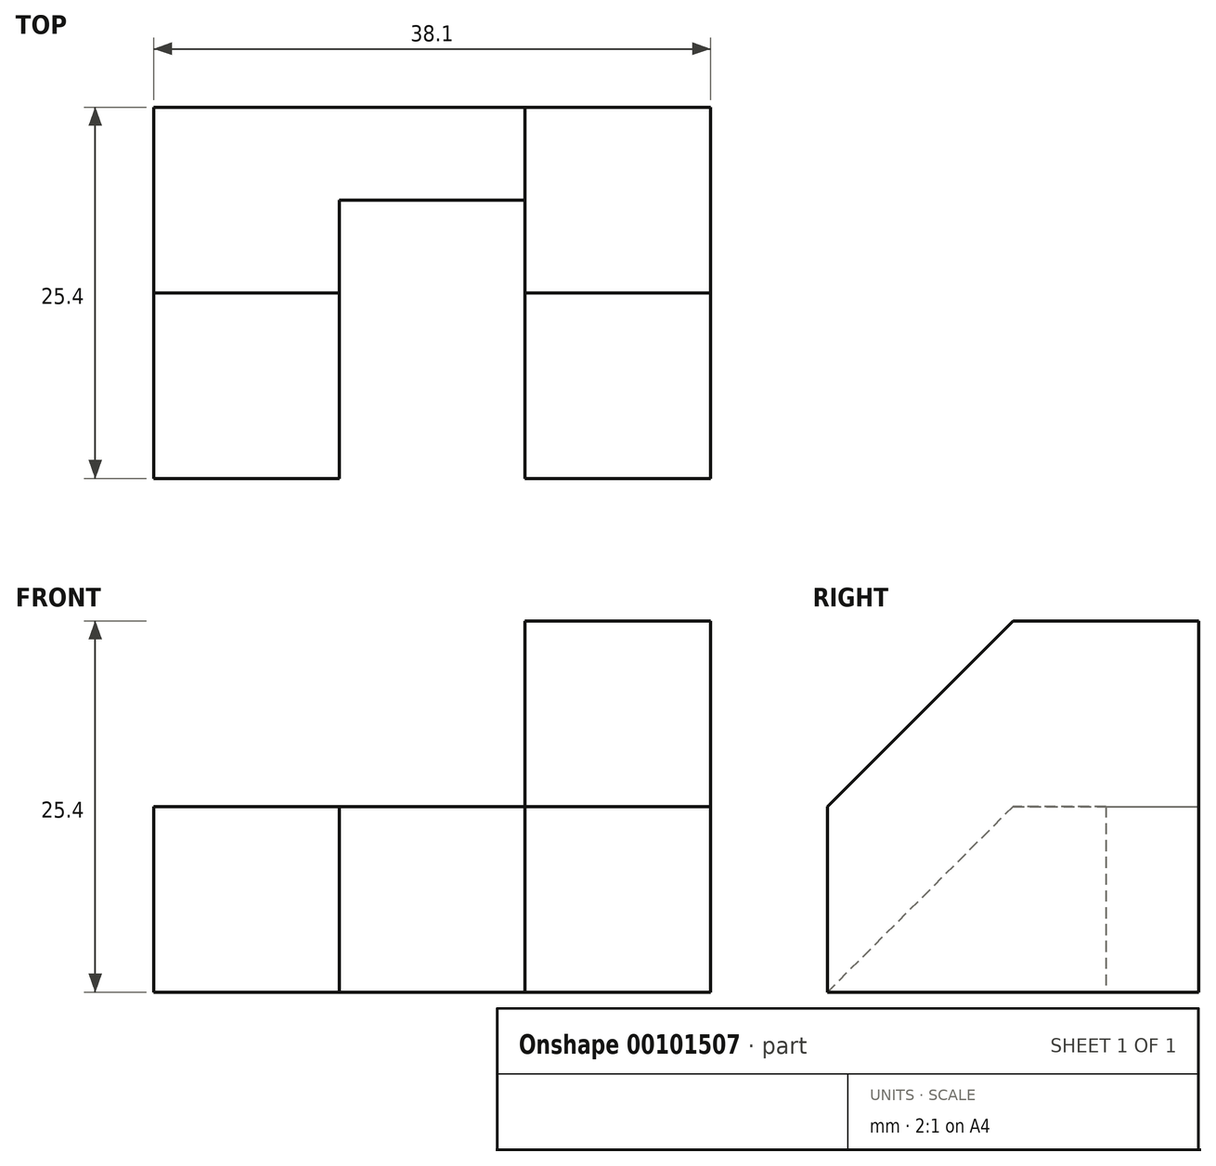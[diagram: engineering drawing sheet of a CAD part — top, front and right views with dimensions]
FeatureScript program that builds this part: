
annotation { "Feature Type Name" : "Feature", "Feature Type Description" : "" }
export const myFeature = defineFeature(function(context is Context, id is Id, definition is map)
    precondition{}
    {
        {
            var Q0;
            Q0=qCreatedBy(makeId("Front.planeOp"),FACE);
            var sketch = newSketch(context, id + "F0", { "sketchPlane" : qUnion([Q0])});
            skLineSegment(sketch, "E0.bottom", {"start": v(0, 0) * mm, "end": v(25.4, 0) * mm});
            skLineSegment(sketch, "E0.top", {"start": v(0, 12.7) * mm, "end": v(25.4, 12.7) * mm});
            skLineSegment(sketch, "E0.left", {"start": v(0, 0) * mm, "end": v(0, 12.7) * mm});
            skLineSegment(sketch, "E0.right", {"start": v(25.4, 0) * mm, "end": v(25.4, 12.7) * mm});
            skSolve(sketch);
        }
        {
            var Q0;
            Q0 = qSketchRegion(id + "F0", true);
            extrude(context, id + "F1", {"entities" : qUnion([Q0]), "endBound" : BoundingType.SYMMETRIC, "depth" : 25.4 * mm});
        }
        {
            var Q0;
            Q0=qCreatedBy(makeId("Front.planeOp"),FACE);
            var sketch = newSketch(context, id + "F2", { "sketchPlane" : qUnion([Q0])});
            skLineSegment(sketch, "E1.bottom", {"start": v(25.4, 0) * mm, "end": v(38.1, 0) * mm});
            skLineSegment(sketch, "E1.top", {"start": v(25.4, 25.4) * mm, "end": v(38.1, 25.4) * mm});
            skLineSegment(sketch, "E1.left", {"start": v(25.4, 0) * mm, "end": v(25.4, 25.4) * mm});
            skLineSegment(sketch, "E1.right", {"start": v(38.1, 0) * mm, "end": v(38.1, 25.4) * mm});
            skSolve(sketch);
        }
        {
            var Q0;
            Q0 = qSketchRegion(id + "F2", true);
            extrude(context, id + "F3", {"entities" : qUnion([Q0]), "operationType" : NewBodyOperationType.ADD, "endBound" : BoundingType.SYMMETRIC, "depth" : 25.4 * mm});
        }
        {
            var Q0;
            Q0=qCreatedBy(makeId("Right.planeOp"),FACE);
            var sketch = newSketch(context, id + "F4", { "sketchPlane" : qUnion([Q0])});
            skLineSegment(sketch, "E2", {"start": v(0, 12.7) * mm, "end": v(-12.7, 0) * mm});
            skLineSegment(sketch, "E3", {"start": v(-12.7, 0) * mm, "end": v(-12.7, 12.7) * mm});
            skLineSegment(sketch, "E4", {"start": v(-12.7, 12.7) * mm, "end": v(0, 12.7) * mm});
            skSolve(sketch);
        }
        {
            var Q0;
            Q0 = qSketchRegion(id + "F4", true);
            extrude(context, id + "F5", {"entities" : qUnion([Q0]), "operationType" : NewBodyOperationType.REMOVE, "depth" : 12.7 * mm});
        }
        {
            var Q0;
            Q0=qCreatedBy(makeId("Top.planeOp"),FACE);
            var sketch = newSketch(context, id + "F6", { "sketchPlane" : qUnion([Q0])});
            skLineSegment(sketch, "E5.bottom", {"start": v(12.7, -12.7) * mm, "end": v(25.4, -12.7) * mm});
            skLineSegment(sketch, "E5.top", {"start": v(12.7, 6.35) * mm, "end": v(25.4, 6.35) * mm});
            skLineSegment(sketch, "E5.left", {"start": v(12.7, -12.7) * mm, "end": v(12.7, 6.35) * mm});
            skLineSegment(sketch, "E5.right", {"start": v(25.4, -12.7) * mm, "end": v(25.4, 6.35) * mm});
            skSolve(sketch);
        }
        {
            var Q0;
            Q0 = qSketchRegion(id + "F6", true);
            extrude(context, id + "F7", {"entities" : qUnion([Q0]), "operationType" : NewBodyOperationType.REMOVE, "depth" : 25.4 * mm});
        }
        {
            var Q0;
            Q0=qCreatedBy(makeId("Right.planeOp"),FACE);
            var sketch = newSketch(context, id + "F8", { "sketchPlane" : qUnion([Q0])});
            skLineSegment(sketch, "E6", {"start": v(0, 25.4) * mm, "end": v(-12.7, 12.7) * mm});
            skLineSegment(sketch, "E7", {"start": v(-12.7, 12.7) * mm, "end": v(-12.7, 25.4) * mm});
            skLineSegment(sketch, "E8", {"start": v(-12.7, 25.4) * mm, "end": v(0, 25.4) * mm});
            skSolve(sketch);
        }
        {
            var Q0;
            Q0 = qSketchRegion(id + "F8", true);
            extrude(context, id + "F9", {"entities" : qUnion([Q0]), "operationType" : NewBodyOperationType.REMOVE, "depth" : 40.66 * mm});
        }
    });
